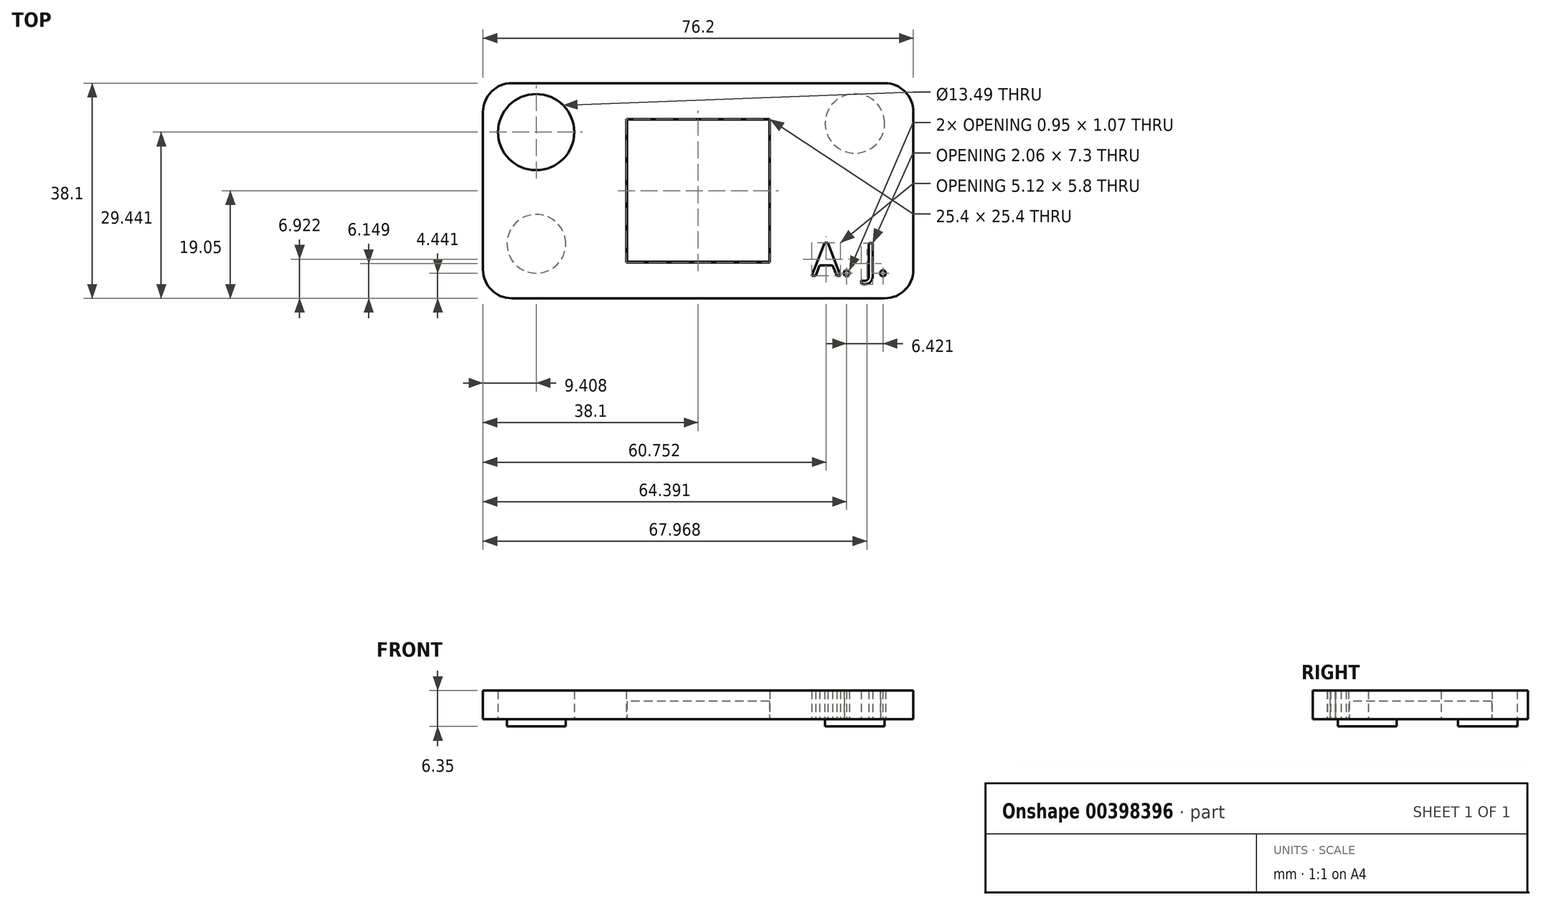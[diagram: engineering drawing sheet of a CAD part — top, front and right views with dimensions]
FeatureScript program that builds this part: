
annotation { "Feature Type Name" : "Feature", "Feature Type Description" : "" }
export const myFeature = defineFeature(function(context is Context, id is Id, definition is map)
    precondition{}
    {
        {
            var Q0;
            Q0=qCreatedBy(makeId("Top.planeOp"),FACE);
            var sketch = newSketch(context, id + "F0", { "sketchPlane" : qUnion([Q0])});
            skLineSegment(sketch, "E0.bottom", {"start": v(38.1, 19.05) * mm, "end": v(-38.1, 19.05) * mm});
            skLineSegment(sketch, "E0.top", {"start": v(38.1, -19.05) * mm, "end": v(-38.1, -19.05) * mm});
            skLineSegment(sketch, "E0.left", {"start": v(38.1, 19.05) * mm, "end": v(38.1, -19.05) * mm});
            skLineSegment(sketch, "E0.right", {"start": v(-38.1, 19.05) * mm, "end": v(-38.1, -19.05) * mm});
            skPoint(sketch, "E0.middle", {"position": v(0, 0) * mm});
            skCircle(sketch, "E1", {"center": v(-28.7, 10.4) * mm, "radius": 6.74 * mm});
            skPoint(sketch, "E1.first.point", {"position": v(-23.34, 6.28) * mm});
            skPoint(sketch, "E1.second.point", {"position": v(-35.08, 12.54) * mm});
            skPoint(sketch, "E1.third.point", {"position": v(-22.2, 8.57) * mm});
            skLineSegment(sketch, "E2.bottom", {"start": v(12.7, 12.7) * mm, "end": v(-12.7, 12.7) * mm});
            skLineSegment(sketch, "E2.top", {"start": v(12.7, -12.7) * mm, "end": v(-12.7, -12.7) * mm});
            skLineSegment(sketch, "E2.left", {"start": v(12.7, 12.7) * mm, "end": v(12.7, -12.7) * mm});
            skLineSegment(sketch, "E2.right", {"start": v(-12.7, 12.7) * mm, "end": v(-12.7, -12.7) * mm});
            skText(sketch, "E3", { "text": "A. J.", "fontName": "OpenSans-Regular.ttf"});
            const initialGuessF0  = {"E3": [0.02009, -0.01503, 1, 0, 0.00583]};
            skSetInitialGuess(sketch, initialGuessF0);
            skSolve(sketch);
        }
        {
            var Q0;
            Q0=makeQuery(id+"F0.imprint","IMPRINT",FACE,{"disambiguationData":[TD([[makeQuery(id+"F0.imprint","IMPRINT",EDGE,{"derivedFrom":sQuery(id+"F0.wireOp",EDGE,"E0.bottom")}),1.0]])]});
            extrude(context, id + "F1", {"entities" : qUnion([Q0]), "depth" : 5.08 * mm});
        }
        {
            var Q0;
            Q0=qCreatedBy(makeId("Top.planeOp"),FACE);
            var sketch = newSketch(context, id + "F2", { "sketchPlane" : qUnion([Q0])});
            skLineSegment(sketch, "E4.bottom", {"start": v(11.9, 11.9) * mm, "end": v(-11.9, 11.9) * mm});
            skLineSegment(sketch, "E4.top", {"start": v(11.9, -11.9) * mm, "end": v(-11.9, -11.9) * mm});
            skLineSegment(sketch, "E4.left", {"start": v(11.9, 11.9) * mm, "end": v(11.9, -11.9) * mm});
            skLineSegment(sketch, "E4.right", {"start": v(-11.9, 11.9) * mm, "end": v(-11.9, -11.9) * mm});
            skPoint(sketch, "E4.middle", {"position": v(0, 0) * mm});
            skSolve(sketch);
        }
        {
            var Q0;
            Q0=makeQuery(id+"F2.imprint","IMPRINT",FACE,{"disambiguationData":[TD([[makeQuery(id+"F2.imprint","IMPRINT",EDGE,{"derivedFrom":sQuery(id+"F2.wireOp",EDGE,"E4.bottom")}),1.0]])]});
            extrude(context, id + "F3", {"entities" : qUnion([Q0]), "depth" : 6.35 * mm});
        }
        {
            var Q0;
            Q0=makeQuery(id+"F3.opExtrude","SWEPT_BODY",BODY,{"disambiguationData":[OSD([sQuery(id+"F2.wireOp",EDGE,"E4.bottom"),sQuery(id+"F2.wireOp",EDGE,"E4.top"),sQuery(id+"F2.wireOp",EDGE,"E4.left"),sQuery(id+"F2.wireOp",EDGE,"E4.right")])]});
            deleteBodies(context, id + "F4", {"entities" : qUnion([Q0])});
        }
        {
            var Q0;
            Q0=qCreatedBy(makeId("Top.planeOp"),FACE);
            var sketch = newSketch(context, id + "F5", { "sketchPlane" : qUnion([Q0])});
            skLineSegment(sketch, "E5.bottom", {"start": v(12.6, 12.6) * mm, "end": v(-12.6, 12.6) * mm});
            skLineSegment(sketch, "E5.top", {"start": v(12.6, -12.6) * mm, "end": v(-12.6, -12.6) * mm});
            skLineSegment(sketch, "E5.left", {"start": v(12.6, 12.6) * mm, "end": v(12.6, -12.6) * mm});
            skLineSegment(sketch, "E5.right", {"start": v(-12.6, 12.6) * mm, "end": v(-12.6, -12.6) * mm});
            skPoint(sketch, "E5.middle", {"position": v(0, 0) * mm});
            skSolve(sketch);
        }
        {
            var Q0;
            Q0=makeQuery(id+"F5.imprint","IMPRINT",FACE,{"disambiguationData":[TD([[makeQuery(id+"F5.imprint","IMPRINT",EDGE,{"derivedFrom":sQuery(id+"F5.wireOp",EDGE,"E5.bottom")}),1.0]])]});
            extrude(context, id + "F6", {"entities" : qUnion([Q0]), "depth" : 3.17 * mm});
        }
        {
            var Q0;
            Q0=qCreatedBy(makeId("Top.planeOp"),FACE);
            var sketch = newSketch(context, id + "F7", { "sketchPlane" : qUnion([Q0])});
            skCircle(sketch, "E6", {"center": v(27.74, 11.92) * mm, "radius": 5.26 * mm});
            skSolve(sketch);
        }
        {
            var Q0;
            Q0=makeQuery(id+"F7.imprint","IMPRINT",FACE,{"disambiguationData":[TD([[makeQuery(id+"F7.imprint","IMPRINT",EDGE,{"derivedFrom":sQuery(id+"F7.wireOp",EDGE,"E6")}),1.0]])]});
            extrude(context, id + "F8", {"entities" : qUnion([Q0]), "operationType" : NewBodyOperationType.ADD, "oppositeDirection" : true, "depth" : 1.27 * mm});
        }
        {
            var Q0;
            Q0=qCreatedBy(makeId("Top.planeOp"),FACE);
            var sketch = newSketch(context, id + "F9", { "sketchPlane" : qUnion([Q0])});
            skCircle(sketch, "E7", {"center": v(-28.66, -9.4) * mm, "radius": 5.2 * mm});
            skSolve(sketch);
        }
        {
            var Q0;
            Q0=makeQuery(id+"F9.imprint","IMPRINT",FACE,{"disambiguationData":[TD([[makeQuery(id+"F9.imprint","IMPRINT",EDGE,{"derivedFrom":sQuery(id+"F9.wireOp",EDGE,"E7")}),1.0]])]});
            extrude(context, id + "F10", {"entities" : qUnion([Q0]), "operationType" : NewBodyOperationType.ADD, "oppositeDirection" : true, "depth" : 1.27 * mm});
        }
        {
            var Q0;
            Q0=makeQuery(id+"F1.opExtrude","SWEPT_EDGE",EDGE,{"disambiguationData":[OSD([sQuery(id+"F0.wireOp",EDGE,"E0.bottom"),sQuery(id+"F0.wireOp",EDGE,"E0.left")])]});
            var Q1;
            Q1=makeQuery(id+"F1.opExtrude","SWEPT_EDGE",EDGE,{"disambiguationData":[OSD([sQuery(id+"F0.wireOp",EDGE,"E0.top"),sQuery(id+"F0.wireOp",EDGE,"E0.left")])]});
            var Q2;
            Q2=makeQuery(id+"F1.opExtrude","SWEPT_EDGE",EDGE,{"disambiguationData":[OSD([sQuery(id+"F0.wireOp",EDGE,"E0.top"),sQuery(id+"F0.wireOp",EDGE,"E0.right")])]});
            var Q3;
            Q3=makeQuery(id+"F1.opExtrude","SWEPT_EDGE",EDGE,{"disambiguationData":[OSD([sQuery(id+"F0.wireOp",EDGE,"E0.bottom"),sQuery(id+"F0.wireOp",EDGE,"E0.right")])]});
            fillet(context, id + "F11", {"entities" : qUnion([Q0, Q1, Q2, Q3]), "radius" : 5.08 * mm, "tangentPropagation" : true, "allowEdgeOverflow" : false});
        }
    });
